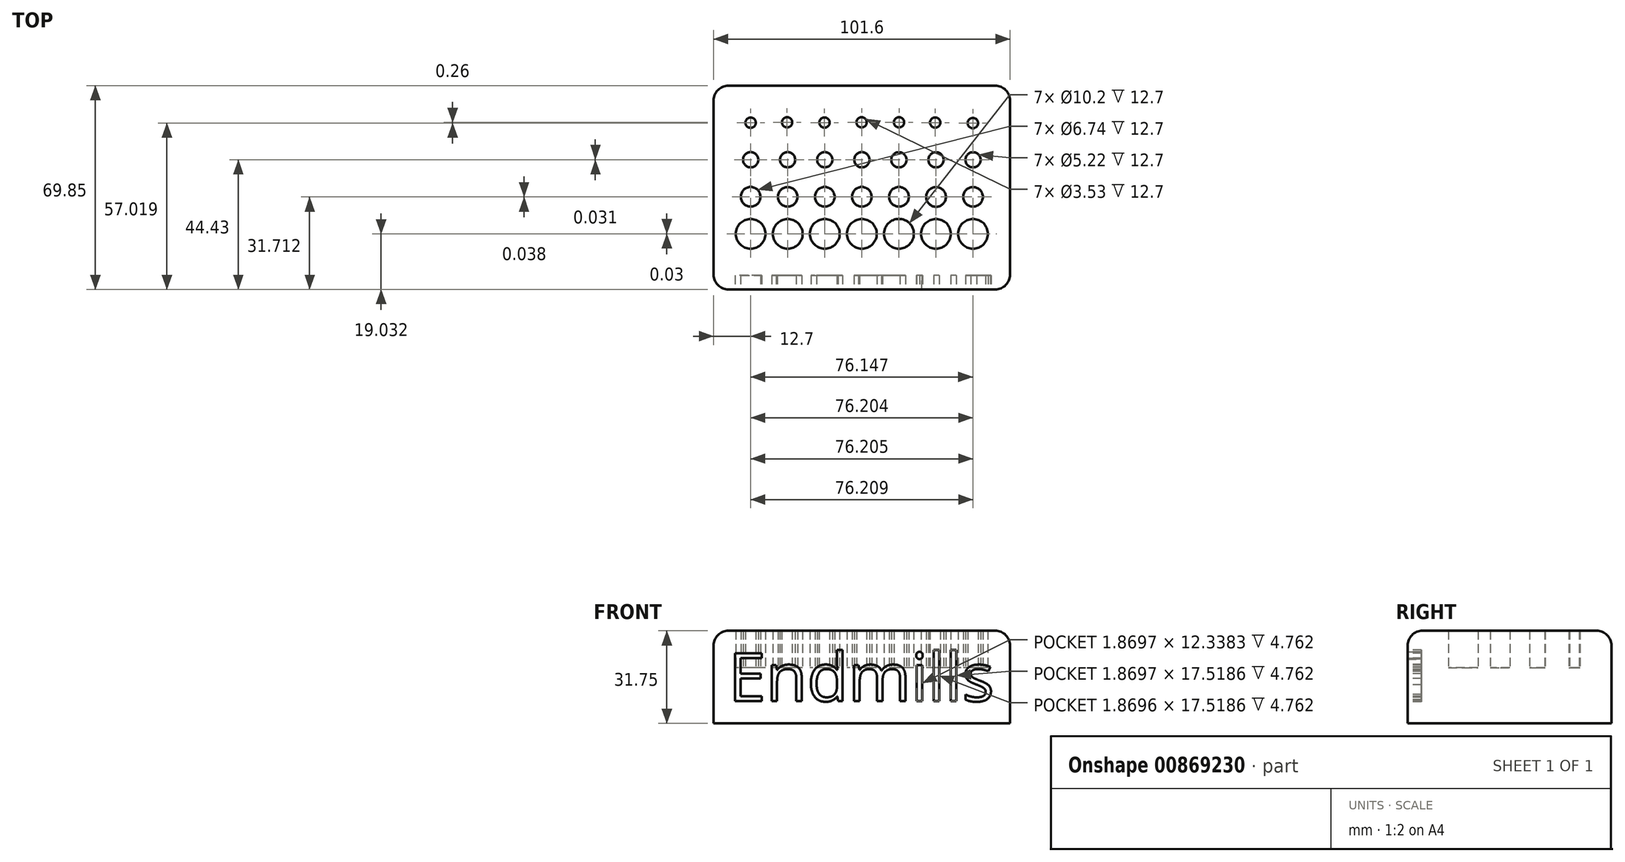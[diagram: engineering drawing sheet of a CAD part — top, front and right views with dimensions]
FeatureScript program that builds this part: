
annotation { "Feature Type Name" : "Feature", "Feature Type Description" : "" }
export const myFeature = defineFeature(function(context is Context, id is Id, definition is map)
    precondition{}
    {
        {
            var Q0;
            Q0=qCreatedBy(makeId("Top.planeOp"),FACE);
            var sketch = newSketch(context, id + "F0", { "sketchPlane" : qUnion([Q0])});
            skLineSegment(sketch, "E0.bottom", {"start": v(0, 0) * mm, "end": v(101.6, 0) * mm});
            skLineSegment(sketch, "E0.top", {"start": v(0, -69.85) * mm, "end": v(101.6, -69.85) * mm});
            skLineSegment(sketch, "E0.left", {"start": v(0, 0) * mm, "end": v(0, -69.85) * mm});
            skLineSegment(sketch, "E0.right", {"start": v(101.6, 0) * mm, "end": v(101.6, -69.85) * mm});
            skSolve(sketch);
        }
        {
            var Q0;
            Q0=makeQuery(id+"F0.imprint","IMPRINT",FACE,{"disambiguationData":[TD([[makeQuery(id+"F0.imprint","IMPRINT",EDGE,{"derivedFrom":sQuery(id+"F0.wireOp",EDGE,"E0.bottom")}),-1.0]])]});
            extrude(context, id + "F1", {"entities" : qUnion([Q0]), "depth" : 19.05 * mm, "offsetDistance" : 25.4 * mm});
        }
        {
            var Q0;
            Q0=makeQuery(id+"F1.opExtrude","SWEPT_EDGE",EDGE,{"disambiguationData":[OSD([sQuery(id+"F0.wireOp",EDGE,"E0.top"),sQuery(id+"F0.wireOp",EDGE,"E0.right")])]});
            var Q1;
            Q1=makeQuery(id+"F1.opExtrude","SWEPT_EDGE",EDGE,{"disambiguationData":[OSD([sQuery(id+"F0.wireOp",EDGE,"E0.top"),sQuery(id+"F0.wireOp",EDGE,"E0.left")])]});
            fillet(context, id + "F2", {"entities" : qUnion([Q0, Q1]), "radius" : 5.08 * mm, "tangentPropagation" : true, "allowEdgeOverflow" : false});
        }
        {
            var Q0;
            Q0=makeQuery(id+"F1.opExtrude","SWEPT_EDGE",EDGE,{"disambiguationData":[OSD([sQuery(id+"F0.wireOp",EDGE,"E0.bottom"),sQuery(id+"F0.wireOp",EDGE,"E0.left")])]});
            var Q1;
            Q1=makeQuery(id+"F1.opExtrude","SWEPT_EDGE",EDGE,{"disambiguationData":[OSD([sQuery(id+"F0.wireOp",EDGE,"E0.bottom"),sQuery(id+"F0.wireOp",EDGE,"E0.right")])]});
            fillet(context, id + "F3", {"entities" : qUnion([Q0, Q1]), "radius" : 5.08 * mm, "tangentPropagation" : true, "allowEdgeOverflow" : false});
        }
        {
            var Q0;
            Q0=makeQuery(id+"F1.opExtrude","CAP_FACE",FACE,{"disambiguationData":[OSD([sQuery(id+"F0.wireOp",EDGE,"E0.bottom"),sQuery(id+"F0.wireOp",EDGE,"E0.top"),sQuery(id+"F0.wireOp",EDGE,"E0.left"),sQuery(id+"F0.wireOp",EDGE,"E0.right")])],"isStart":false});
            var sketch = newSketch(context, id + "F4", { "sketchPlane" : qUnion([Q0])});
            skCircle(sketch, "E1", {"center": v(12.7, -12.7) * mm, "radius": 1.77 * mm});
            skCircle(sketch, "E2", {"center": v(25.18, -12.57) * mm, "radius": 1.77 * mm});
            skCircle(sketch, "E3", {"center": v(38, -12.66) * mm, "radius": 1.77 * mm});
            skCircle(sketch, "E4", {"center": v(50.73, -12.57) * mm, "radius": 1.77 * mm});
            skCircle(sketch, "E5", {"center": v(63.55, -12.57) * mm, "radius": 1.77 * mm});
            skCircle(sketch, "E6", {"center": v(75.94, -12.66) * mm, "radius": 1.77 * mm});
            skCircle(sketch, "E7", {"center": v(88.85, -12.83) * mm, "radius": 1.77 * mm});
            skCircle(sketch, "E8", {"center": v(12.7, -25.4) * mm, "radius": 2.6 * mm});
            skCircle(sketch, "E9", {"center": v(25.37, -25.4) * mm, "radius": 2.6 * mm});
            skCircle(sketch, "E10", {"center": v(38.1, -25.39) * mm, "radius": 2.6 * mm});
            skCircle(sketch, "E11", {"center": v(50.8, -25.4) * mm, "radius": 2.6 * mm});
            skCircle(sketch, "E12", {"center": v(63.5, -25.42) * mm, "radius": 2.6 * mm});
            skCircle(sketch, "E13", {"center": v(76.22, -25.42) * mm, "radius": 2.6 * mm});
            skCircle(sketch, "E14", {"center": v(88.9, -25.42) * mm, "radius": 2.6 * mm});
            skCircle(sketch, "E15", {"center": v(12.7, -38.1) * mm, "radius": 3.37 * mm});
            skCircle(sketch, "E16", {"center": v(25.39, -38.12) * mm, "radius": 3.37 * mm});
            skCircle(sketch, "E17", {"center": v(38.1, -38.1) * mm, "radius": 3.37 * mm});
            skCircle(sketch, "E18", {"center": v(50.8, -38.1) * mm, "radius": 3.37 * mm});
            skCircle(sketch, "E19", {"center": v(63.52, -38.1) * mm, "radius": 3.37 * mm});
            skCircle(sketch, "E20", {"center": v(76.23, -38.14) * mm, "radius": 3.37 * mm});
            skCircle(sketch, "E21", {"center": v(88.9, -38.12) * mm, "radius": 3.37 * mm});
            skCircle(sketch, "E22", {"center": v(12.7, -50.8) * mm, "radius": 5.1 * mm});
            skCircle(sketch, "E23", {"center": v(25.41, -50.82) * mm, "radius": 5.1 * mm});
            skCircle(sketch, "E24", {"center": v(38.11, -50.8) * mm, "radius": 5.1 * mm});
            skCircle(sketch, "E25", {"center": v(50.81, -50.8) * mm, "radius": 5.1 * mm});
            skCircle(sketch, "E26", {"center": v(63.52, -50.79) * mm, "radius": 5.1 * mm});
            skCircle(sketch, "E27", {"center": v(76.2, -50.8) * mm, "radius": 5.1 * mm});
            skCircle(sketch, "E28", {"center": v(88.9, -50.8) * mm, "radius": 5.1 * mm});
            skSolve(sketch);
        }
        {
            var Q0;
            Q0=makeQuery(id+"F4.imprint","IMPRINT",FACE,{"disambiguationData":[TD([[makeQuery(id+"F4.imprint","IMPRINT",EDGE,{"derivedFrom":sQuery(id+"F4.wireOp",EDGE,"E1")}),-1.0]])]});
            extrude(context, id + "F5", {"entities" : qUnion([Q0]), "operationType" : NewBodyOperationType.ADD, "depth" : 12.7 * mm, "offsetDistance" : 25.4 * mm});
        }
        {
            var Q0;
            Q0=makeQuery(id+"F5.opExtrude","CAP_EDGE",EDGE,{"disambiguationData":[OSD([sQuery(id+"F0.wireOp",EDGE,"E0.top")])],"isStart":false});
            fillet(context, id + "F6", {"entities" : qUnion([Q0]), "radius" : 5.08 * mm, "tangentPropagation" : true, "allowEdgeOverflow" : false});
        }
        {
            var Q0;
            {var subQ0=sQuery(id+"F0.wireOp",EDGE,"E0.top");Q0=makeQuery(id+"F5.boolean.opBoolean","MERGE",FACE,{"derivedFrom":[makeQuery(id+"F1.opExtrude","SWEPT_FACE",FACE,{"disambiguationData":[OSD([subQ0])]}),makeQuery(id+"F5.opExtrude","SWEPT_FACE",FACE,{"disambiguationData":[OSD([subQ0])]})]});}
            var sketch = newSketch(context, id + "F7", { "sketchPlane" : qUnion([Q0])});
            skText(sketch, "E29", { "text": "Endmills\n", "fontName": "OpenSans-Regular.ttf"});
            const initialGuessF7  = {"E29": [0.00508, 0.0076, 1, 0, 0.0166]};
            skSetInitialGuess(sketch, initialGuessF7);
            skSolve(sketch);
        }
        {
            var Q0;
            Q0 = qSketchRegion(id + "F7", true);
            extrude(context, id + "F8", {"entities" : qUnion([Q0]), "operationType" : NewBodyOperationType.REMOVE, "oppositeDirection" : true, "depth" : 4.76 * mm, "offsetDistance" : 25.4 * mm});
        }
    });
